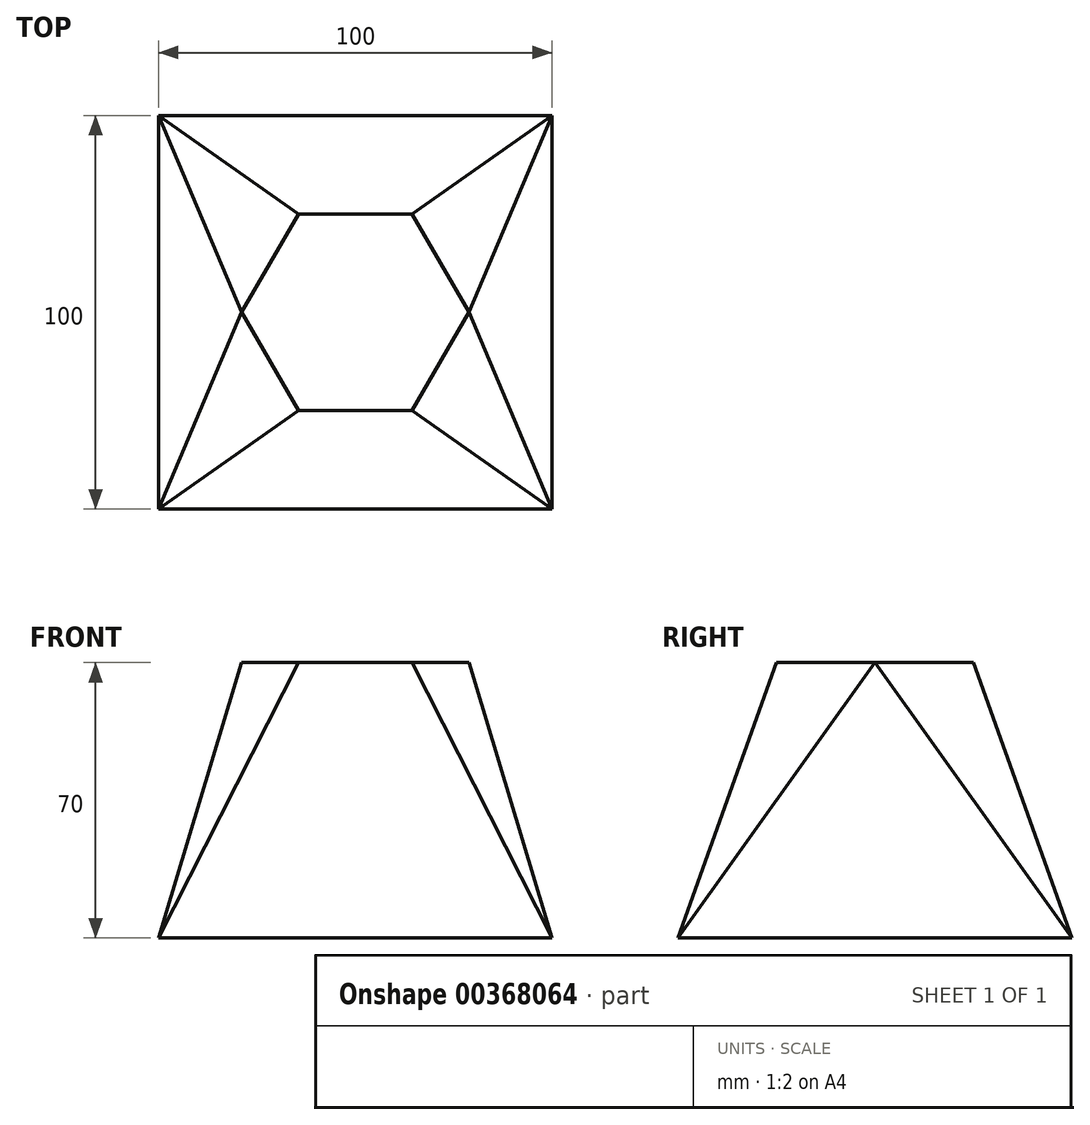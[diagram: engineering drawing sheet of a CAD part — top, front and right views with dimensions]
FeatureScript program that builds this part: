
annotation { "Feature Type Name" : "Feature", "Feature Type Description" : "" }
export const myFeature = defineFeature(function(context is Context, id is Id, definition is map)
    precondition{}
    {
        {
            var Q0;
            Q0=qCreatedBy(makeId("Top.planeOp"),FACE);
            var sketch = newSketch(context, id + "F0", { "sketchPlane" : qUnion([Q0])});
            skLineSegment(sketch, "E0.bottom", {"start": v(50, -50) * mm, "end": v(-50, -50) * mm});
            skLineSegment(sketch, "E0.top", {"start": v(50, 50) * mm, "end": v(-50, 50) * mm});
            skLineSegment(sketch, "E0.left", {"start": v(50, -50) * mm, "end": v(50, 50) * mm});
            skLineSegment(sketch, "E0.right", {"start": v(-50, -50) * mm, "end": v(-50, 50) * mm});
            skPoint(sketch, "E0.middle", {"position": v(0, 0) * mm});
            skSolve(sketch);
        }
        {
            var Q0;
            Q0=qCreatedBy(makeId("Top.planeOp"),FACE);
            cPlane(context, id + "F1", {"entities" : qUnion([Q0]), "cplaneType" : CPlaneType.OFFSET, "offset" : 70 * mm, "width" : 150 * mm, "height" : 150 * mm});
        }
        {
            var Q0;
            Q0=qCreatedBy(id+"F1.planeOp",FACE);
            var sketch = newSketch(context, id + "F2", { "sketchPlane" : qUnion([Q0])});
            skCircle(sketch, "E1.cCircle", {"center": v(0, 0) * mm, "radius": 25 * mm, "construction": true});
            skLineSegment(sketch, "E1.0", {"start": v(-14.43, 25) * mm, "end": v(14.43, 25) * mm});
            skLineSegment(sketch, "E1.1", {"start": v(14.43, 25) * mm, "end": v(28.87, 0) * mm});
            skLineSegment(sketch, "E1.2", {"start": v(28.87, 0) * mm, "end": v(14.43, -25) * mm});
            skLineSegment(sketch, "E1.3", {"start": v(14.43, -25) * mm, "end": v(-14.43, -25) * mm});
            skLineSegment(sketch, "E1.4", {"start": v(-14.43, -25) * mm, "end": v(-28.87, 0) * mm});
            skLineSegment(sketch, "E1.5", {"start": v(-28.87, 0) * mm, "end": v(-14.43, 25) * mm});
            skPoint(sketch, "E1.0.midPoint", {"position": v(0, 25) * mm});
            skLineSegment(sketch, "E2", {"start": v(-14.43, 25) * mm, "end": v(-14.43, -25) * mm});
            skLineSegment(sketch, "E3", {"start": v(14.43, 25) * mm, "end": v(14.43, -25) * mm});
            skSolve(sketch);
        }
        {
            var Q0;
            Q0=makeQuery(id+"F2.imprint","IMPRINT",FACE,{"disambiguationData":[TD([[makeQuery(id+"F2.imprint","IMPRINT",EDGE,{"derivedFrom":sQuery(id+"F2.wireOp",EDGE,"E1.0")}),-1.0]])]});
            var Q1;
            Q1=makeQuery(id+"F0.imprint","IMPRINT",FACE,{"disambiguationData":[TD([[makeQuery(id+"F0.imprint","IMPRINT",EDGE,{"derivedFrom":sQuery(id+"F0.wireOp",EDGE,"E0.bottom")}),-1.0]])]});
            loft(context, id + "F3", {"sheetProfilesArray" : [{ "sheetProfileEntities" : qUnion([Q0]) }, { "sheetProfileEntities" : qUnion([Q1]) }]});
        }
        {
            var Q1;
            Q1=makeQuery(id+"F2.imprint","IMPRINT",FACE,{"disambiguationData":[TD([[makeQuery(id+"F2.imprint","IMPRINT",EDGE,{"derivedFrom":sQuery(id+"F2.wireOp",EDGE,"E1.4")}),-1.0]])]});
            var Q2;
            Q2=sQuery(id+"F0.wireOp",VERTEX,"E0.right.end");
            loft(context, id + "F4", {"operationType" : NewBodyOperationType.ADD, "sheetProfilesArray" : [{ "sheetProfileEntities" : qUnion([Q1]) }, { "sheetProfileEntities" : qUnion([Q2]) }]});
        }
        {
            var Q1;
            Q1=makeQuery(id+"F2.imprint","IMPRINT",FACE,{"disambiguationData":[TD([[makeQuery(id+"F2.imprint","IMPRINT",EDGE,{"derivedFrom":sQuery(id+"F2.wireOp",EDGE,"E1.4")}),-1.0]])]});
            var Q2;
            Q2=sQuery(id+"F0.wireOp",VERTEX,"E0.right.start");
            loft(context, id + "F5", {"operationType" : NewBodyOperationType.ADD, "sheetProfilesArray" : [{ "sheetProfileEntities" : qUnion([Q1]) }, { "sheetProfileEntities" : qUnion([Q2]) }]});
        }
        {
            var Q1;
            Q1=makeQuery(id+"F4.opLoft","SWEPT_FACE",FACE,{"disambiguationData":[OSD([sQuery(id+"F2.wireOp",EDGE,"E1.3"),sQuery(id+"F2.wireOp",EDGE,"E1.4"),sQuery(id+"F2.wireOp",EDGE,"E1.5"),sQuery(id+"F2.wireOp",EDGE,"E2")])]});
            var Q2;
            Q2=makeQuery(id+"F5.opLoft","SWEPT_FACE",FACE,{"disambiguationData":[OSD([sQuery(id+"F2.wireOp",EDGE,"E1.0"),sQuery(id+"F2.wireOp",EDGE,"E1.4"),sQuery(id+"F2.wireOp",EDGE,"E1.5"),sQuery(id+"F2.wireOp",EDGE,"E2")])]});
            var Q3;
            Q3=sQuery(id+"F0.wireOp",VERTEX,"E0.right.start");
            var Q4;
            Q4=sQuery(id+"F0.wireOp",VERTEX,"E0.right.end");
            loft(context, id + "F6", {"operationType" : NewBodyOperationType.ADD, "sheetProfilesArray" : [{ "sheetProfileEntities" : qUnion([Q1]) }, { "sheetProfileEntities" : qUnion([Q2]) }], "matchConnections" : true, "connections" : [{ "connectionEntities" : qUnion([Q3, Q4]), "connectionEdgeQueries" : qUnion([]), "connectionEdgeParameters" : [] }]});
        }
        {
            var Q1;
            Q1=makeQuery(id+"F2.imprint","IMPRINT",FACE,{"disambiguationData":[TD([[makeQuery(id+"F2.imprint","IMPRINT",EDGE,{"derivedFrom":sQuery(id+"F2.wireOp",EDGE,"E1.1")}),-1.0]])]});
            var Q2;
            Q2=sQuery(id+"F0.wireOp",VERTEX,"E0.left.start");
            loft(context, id + "F7", {"operationType" : NewBodyOperationType.ADD, "sheetProfilesArray" : [{ "sheetProfileEntities" : qUnion([Q1]) }, { "sheetProfileEntities" : qUnion([Q2]) }]});
        }
        {
            var Q1;
            Q1=makeQuery(id+"F2.imprint","IMPRINT",FACE,{"disambiguationData":[TD([[makeQuery(id+"F2.imprint","IMPRINT",EDGE,{"derivedFrom":sQuery(id+"F2.wireOp",EDGE,"E1.1")}),-1.0]])]});
            var Q2;
            Q2=sQuery(id+"F0.wireOp",VERTEX,"E0.left.end");
            loft(context, id + "F8", {"operationType" : NewBodyOperationType.ADD, "sheetProfilesArray" : [{ "sheetProfileEntities" : qUnion([Q1]) }, { "sheetProfileEntities" : qUnion([Q2]) }]});
        }
        {
            var Q1;
            Q1=makeQuery(id+"F8.opLoft","SWEPT_FACE",FACE,{"disambiguationData":[OSD([sQuery(id+"F2.wireOp",EDGE,"E1.1"),sQuery(id+"F2.wireOp",EDGE,"E1.2"),sQuery(id+"F2.wireOp",EDGE,"E1.3"),sQuery(id+"F2.wireOp",EDGE,"E3")])]});
            var Q2;
            Q2=makeQuery(id+"F7.opLoft","SWEPT_FACE",FACE,{"disambiguationData":[OSD([sQuery(id+"F2.wireOp",EDGE,"E1.0"),sQuery(id+"F2.wireOp",EDGE,"E1.1"),sQuery(id+"F2.wireOp",EDGE,"E1.2"),sQuery(id+"F2.wireOp",EDGE,"E3")])]});
            var Q3;
            Q3=sQuery(id+"F0.wireOp",VERTEX,"E0.left.start");
            var Q4;
            Q4=sQuery(id+"F0.wireOp",VERTEX,"E0.left.end");
            loft(context, id + "F9", {"operationType" : NewBodyOperationType.ADD, "sheetProfilesArray" : [{ "sheetProfileEntities" : qUnion([Q1]) }, { "sheetProfileEntities" : qUnion([Q2]) }], "matchConnections" : true, "connections" : [{ "connectionEntities" : qUnion([Q3, Q4]), "connectionEdgeQueries" : qUnion([]), "connectionEdgeParameters" : [] }]});
        }
    });
